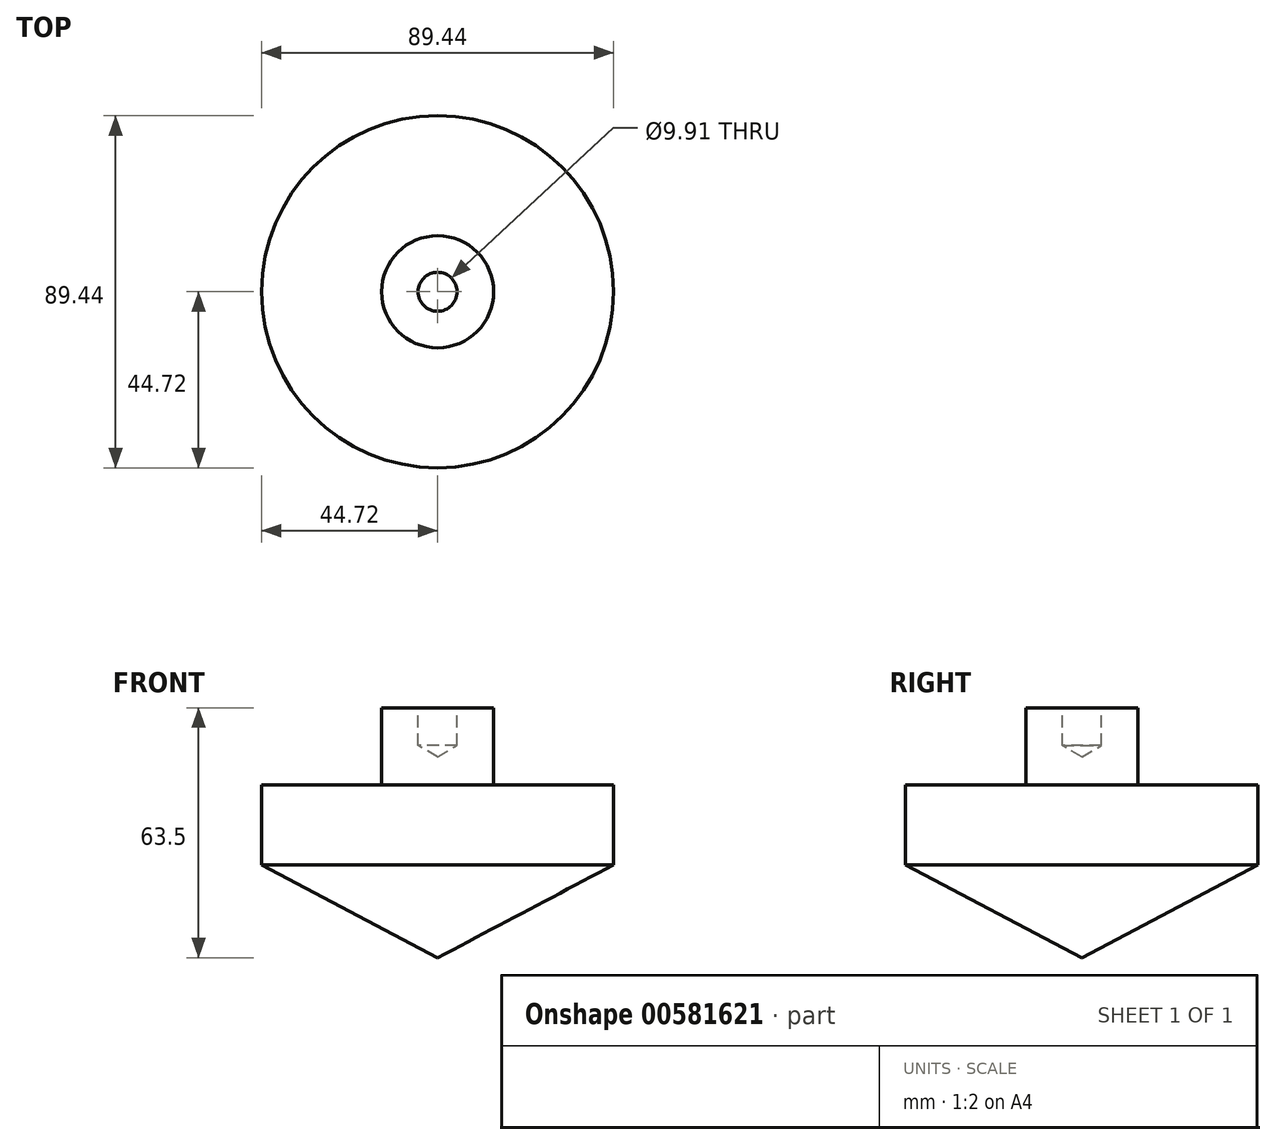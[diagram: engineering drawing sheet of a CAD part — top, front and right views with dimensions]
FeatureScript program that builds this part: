
annotation { "Feature Type Name" : "Feature", "Feature Type Description" : "" }
export const myFeature = defineFeature(function(context is Context, id is Id, definition is map)
    precondition{}
    {
        {
            var Q0;
            Q0=qCreatedBy(makeId("Front.planeOp"),FACE);
            var sketch = newSketch(context, id + "F0", { "sketchPlane" : qUnion([Q0])});
            skLineSegment(sketch, "E0", {"start": v(0, 0) * mm, "end": v(44.72, 23.6) * mm});
            skLineSegment(sketch, "E1", {"start": v(44.72, 23.6) * mm, "end": v(44.72, 43.92) * mm});
            skLineSegment(sketch, "E2", {"start": v(44.72, 43.92) * mm, "end": v(14.24, 43.92) * mm});
            skLineSegment(sketch, "E3", {"start": v(14.24, 43.92) * mm, "end": v(14.24, 63.5) * mm});
            skLineSegment(sketch, "E4", {"start": v(14.24, 63.5) * mm, "end": v(0, 63.5) * mm});
            skLineSegment(sketch, "E5", {"start": v(0, 63.5) * mm, "end": v(0, 0) * mm});
            skSolve(sketch);
        }
        {
            var Q0;
            Q0=makeQuery(id+"F0.imprint","IMPRINT",FACE,{"disambiguationData":[TD([[makeQuery(id+"F0.imprint","IMPRINT",EDGE,{"derivedFrom":sQuery(id+"F0.wireOp",EDGE,"E0")}),1.0]])]});
            var Q1;
            Q1=sQuery(id+"F0.wireOp",EDGE,"E5");
            revolve(context, id + "F1", {"entities" : qUnion([Q0]), "axis" : qUnion([Q1]), "revolveType" : RevolveType.FULL});
        }
        {
            var Q0;
            Q0=makeQuery(id+"F1.opRevolve","SWEPT_FACE",FACE,{"disambiguationData":[OSD([sQuery(id+"F0.wireOp",EDGE,"E4")])]});
            var sketch = newSketch(context, id + "F2", { "sketchPlane" : qUnion([Q0])});
            skPoint(sketch, "E6", {"position": v(0, 0) * mm});
            skSolve(sketch);
        }
        {
            var Q0;
            Q0=sQuery(id+"F2.wireOp",VERTEX,"E6");
            var Q1;
            Q1=makeQuery(id+"F1.opRevolve","SWEPT_BODY",BODY,{"disambiguationData":[OSD([sQuery(id+"F0.wireOp",EDGE,"E0"),sQuery(id+"F0.wireOp",EDGE,"E1"),sQuery(id+"F0.wireOp",EDGE,"E2"),sQuery(id+"F0.wireOp",EDGE,"E3"),sQuery(id+"F0.wireOp",EDGE,"E4"),sQuery(id+"F0.wireOp",EDGE,"E5")])]});
            hole(context, id + "F3", {"style" : HoleStyle.SIMPLE, "endStyle" : HoleEndStyle.BLIND, "holeDiameter" : 9.9 * mm, "majorDiameter" : 6.35 * mm, "holeDepth" : 9.52 * mm, "isTappedThrough" : true, "tappedDepth" : 12.7 * mm, "tapClearance" : 3, "locations" : qUnion([Q0]), "scope" : qUnion([Q1])});
        }
    });
